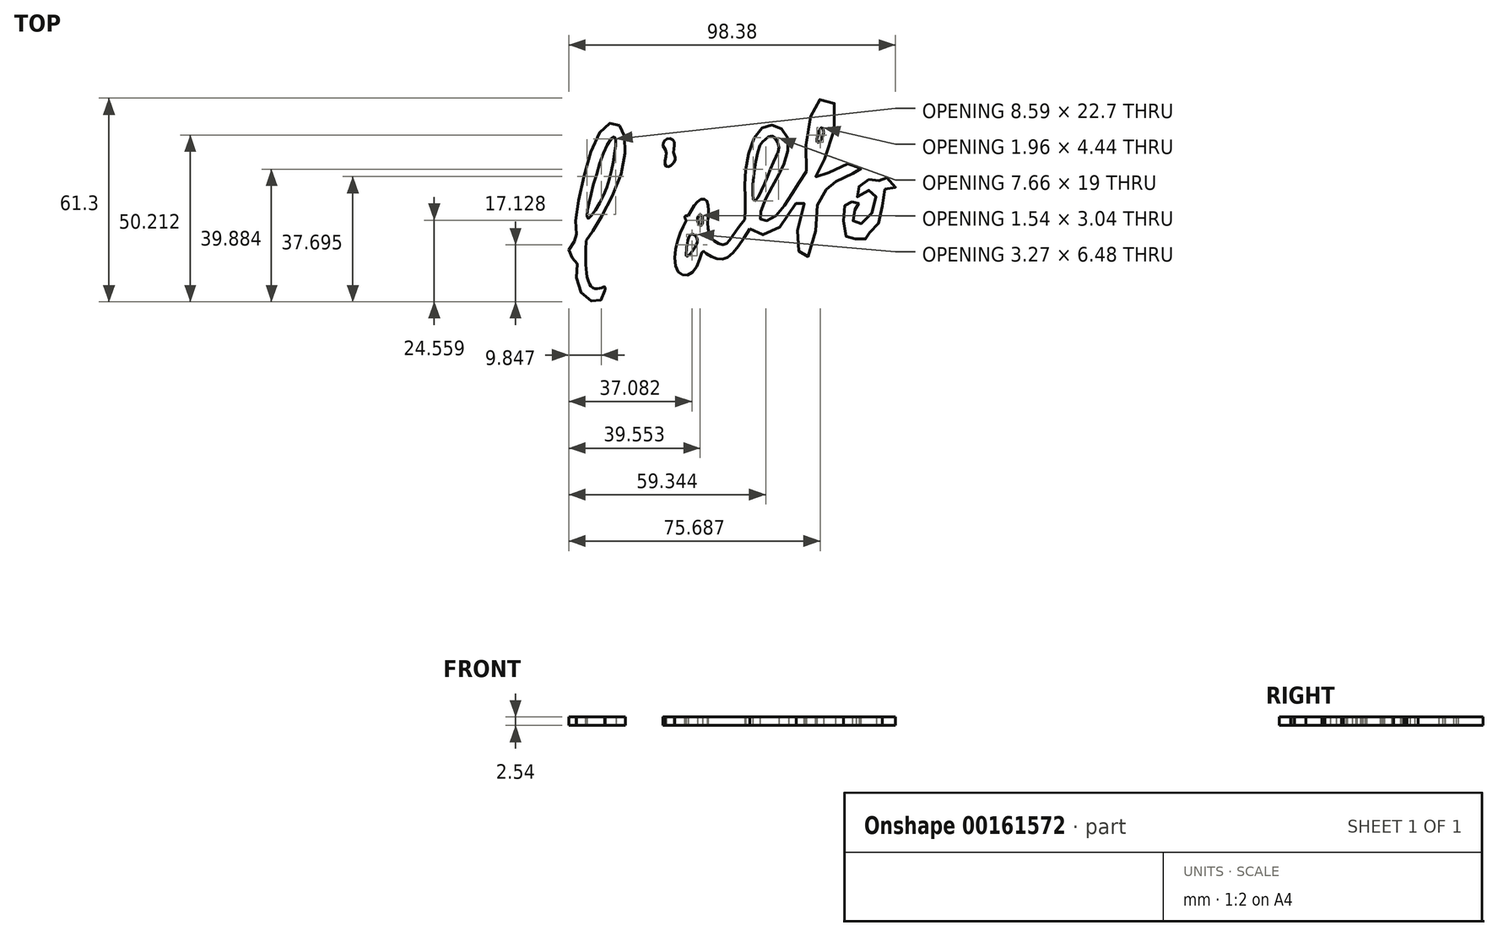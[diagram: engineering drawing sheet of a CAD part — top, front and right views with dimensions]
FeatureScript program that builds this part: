
annotation { "Feature Type Name" : "Feature", "Feature Type Description" : "" }
export const myFeature = defineFeature(function(context is Context, id is Id, definition is map)
    precondition{}
    {
        {
            var Q0;
            Q0=qCreatedBy(makeId("Top.planeOp"),FACE);
            var sketch = newSketch(context, id + "F0", { "sketchPlane" : qUnion([Q0])});
            skFitSpline(sketch, "E0", {"points": [v(-105.2, -43.44) * mm, v(-106.46, -46.35) * mm, v(-110.13, -46.1) * mm, v(-113.68, -40.02) * mm, v(-113.68, -34.32) * mm, v(-115.58, -33.05) * mm, v(-115.58, -30.01) * mm, v(-113.68, -27.73) * mm, v(-113.93, -24.7) * mm, v(-111.65, -9.88) * mm, v(-105.57, 5.7) * mm, v(-101.65, 6.97) * mm, v(-99.37, 3.55) * mm, v(-100.25, -8.23) * mm, v(-107.6, -23.55) * mm, v(-110.76, -28.37) * mm], "startDerivative": vector(-14.94, -73.82) * mm, "endDerivative": vector(-43.32, -62.37) * mm});
            skFitSpline(sketch, "E1", {"points": [v(-110.76, -28.37) * mm, v(-110.9, -34.57) * mm, v(-109.24, -42.17) * mm, v(-106.46, -42.68) * mm, v(-105.06, -42.3) * mm, v(-105.2, -43.44) * mm], "startDerivative": vector(-1.12, -20.77) * mm, "endDerivative": vector(-3.7, -13.08) * mm});
            skFitSpline(sketch, "E2", {"points": [v(-103.3, 2.28) * mm, v(-107.6, -8.23) * mm, v(-110.26, -18.87) * mm, v(-110.26, -21.65) * mm, v(-108.1, -19.38) * mm, v(-104.18, -11.27) * mm, v(-102.28, -2.28) * mm, v(-102.03, 2.79) * mm, v(-103.3, 2.28) * mm]});
            skFitSpline(sketch, "E3", {"points": [v(-87.59, 0.26) * mm, v(-86.7, -1.4) * mm, v(-86.95, -5.57) * mm, v(-85.69, -5.95) * mm, v(-83.91, -3.67) * mm, v(-84.42, -1.64) * mm, v(-84.42, 1.78) * mm, v(-86.7, 2.16) * mm, v(-87.59, 0.26) * mm]});
            skFitSpline(sketch, "E4", {"points": [v(-80.62, -22.41) * mm, v(-83.15, -28.11) * mm, v(-83.66, -36.6) * mm, v(-81, -38.75) * mm, v(-77.7, -36.6) * mm, v(-75.68, -31.53) * mm, v(-74.92, -31.91) * mm, v(-71.5, -33.81) * mm, v(-67.83, -33.18) * mm, v(-61.5, -24.82) * mm], "startDerivative": vector(-21.7, -39.66) * mm, "endDerivative": vector(39, 63) * mm});
            skFitSpline(sketch, "E5", {"points": [v(-80.62, -22.41) * mm, v(-81, -21.02) * mm, v(-79.99, -20.9) * mm], "startDerivative": vector(-1.5, 3.19) * mm, "endDerivative": vector(2.88, -0.25) * mm});
            skFitSpline(sketch, "E6", {"points": [v(-79.99, -20.9) * mm, v(-76.57, -16.08) * mm, v(-74.41, -16.34) * mm, v(-74.16, -22.54) * mm, v(-73.02, -27.48) * mm, v(-69.22, -29.5) * mm, v(-66.3, -26.34) * mm, v(-63.02, -22.03) * mm], "startDerivative": vector(19.66, 38.15) * mm, "endDerivative": vector(22.24, 26.78) * mm});
            skFitSpline(sketch, "E7", {"points": [v(-44.4, -7.47) * mm, v(-44.44, 1.82) * mm, v(-42.23, 11.73) * mm, v(-40.01, 14.3) * mm, v(-36.63, 13.83) * mm, v(-35.81, 6.49) * mm, v(-39.78, -5.29) * mm, v(-41.64, -9.14) * mm, v(-40.01, -9.37) * mm, v(-36.05, -6.69) * mm, v(-30.57, -5.06) * mm, v(-28.12, -5.99) * mm, v(-28.58, -8.32) * mm, v(-30.33, -8.09) * mm, v(-34.88, -9.72) * mm, v(-36.86, -12.29) * mm, v(-38.5, -12.98) * mm, v(-40.94, -16.48) * mm, v(-41.53, -24.06) * mm, v(-43.97, -33.16) * mm, v(-45.14, -31.87) * mm, v(-46.89, -31.4) * mm, v(-47, -24.88) * mm, v(-45.14, -16.25) * mm, v(-46.07, -15.55) * mm, v(-50.97, -22.55) * mm, v(-55.98, -26.4) * mm, v(-59.01, -26.28) * mm, v(-61.5, -24.82) * mm], "startDerivative": vector(-11.09, 174.57) * mm, "endDerivative": vector(-84.35, 59.96) * mm});
            skFitSpline(sketch, "E8", {"points": [v(-79.07, -26.4) * mm, v(-80.58, -31.17) * mm, v(-80.35, -33.04) * mm, v(-78.25, -30.7) * mm, v(-77.32, -27.8) * mm, v(-79.07, -26.4) * mm]});
            skFitSpline(sketch, "E9", {"points": [v(-76.04, -20.68) * mm, v(-77.27, -21.7) * mm, v(-76.1, -23.75) * mm, v(-76.04, -20.68) * mm]});
            skFitSpline(sketch, "E10", {"points": [v(-56.8, 2.17) * mm, v(-58.9, -0.98) * mm, v(-60.3, -16.25) * mm, v(-58.43, -14.27) * mm, v(-54.35, -4.6) * mm, v(-52.72, -0.04) * mm, v(-54.7, 3.1) * mm, v(-56.8, 2.17) * mm]});
            skFitSpline(sketch, "E11", {"points": [v(-39.78, 5.67) * mm, v(-41.06, 3.45) * mm, v(-41.06, 1.24) * mm, v(-39.43, 3.34) * mm, v(-39.78, 5.67) * mm]});
            skFitSpline(sketch, "E12", {"points": [v(-30.68, -16.6) * mm, v(-32.55, -17.18) * mm, v(-33.25, -23.13) * mm, v(-31.73, -27.9) * mm, v(-28.12, -27.56) * mm, v(-26.25, -27.8) * mm, v(-25.2, -25.7) * mm, v(-21.94, -21.61) * mm, v(-20.66, -12.75) * mm, v(-17.64, -12.25) * mm, v(-20.89, -9.25) * mm, v(-22.52, -10.3) * mm, v(-25.32, -9.95) * mm, v(-28.7, -12.17) * mm, v(-29.11, -15.16) * mm, v(-24.85, -12.98) * mm, v(-23.57, -17.18) * mm, v(-27.53, -23.01) * mm, v(-30.1, -23.01) * mm, v(-30.1, -19.4) * mm, v(-28.7, -17.88) * mm, v(-29.05, -16.6) * mm, v(-30.68, -16.6) * mm]});
            skFitSpline(sketch, "E13", {"points": [v(-44.4, -7.47) * mm, v(-49.2, -14.86) * mm, v(-54.6, -21.62) * mm, v(-57.85, -22.2) * mm, v(-58.44, -20.51) * mm, v(-55.05, -12.65) * mm, v(-51.35, -5.56) * mm, v(-50.11, 2.7) * mm, v(-54.14, 6.34) * mm, v(-58.96, 4.46) * mm, v(-62.8, -7.18) * mm, v(-62.8, -16.29) * mm, v(-63.02, -22.03) * mm], "startDerivative": vector(-49.65, -75.15) * mm, "endDerivative": vector(-6.3, -71.96) * mm});
            skSolve(sketch);
        }
        {
            var Q0;
            Q0 = qSketchRegion(id + "F0", true);
            extrude(context, id + "F1", {"entities" : qUnion([Q0]), "depth" : 2.54 * mm});
        }
    });
